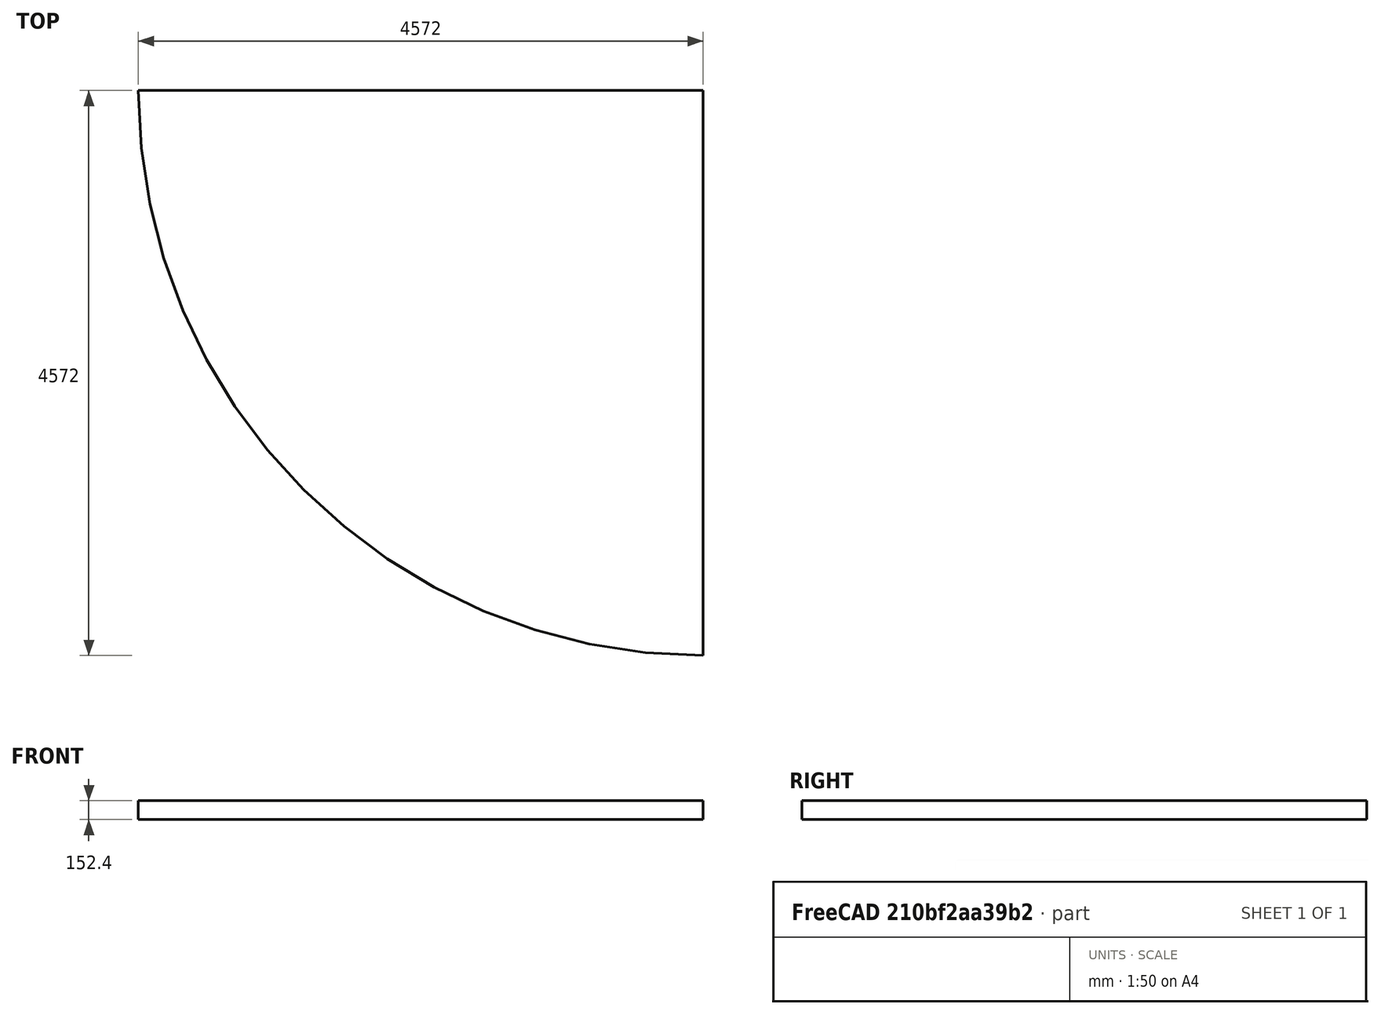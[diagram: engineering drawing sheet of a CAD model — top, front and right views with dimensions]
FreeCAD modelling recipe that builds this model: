
FCSTD DOCUMENT  (FreeCAD 0.20R29177 (Git))
Label: pad
License: All rights reserved
LicenseURL: http://en.wikipedia.org/wiki/All_rights_reserved
objects: Sketcher::SketchObject×1, PartDesign::Pad×1, PartDesign::Body×1
note: 4 computed .brp shape members not serialized (recipe doc carries the construction recipe); baked Part::Feature solids carry a one-line shape summary decoded from their .brp

FEATURE [Sketcher::SketchObject] Sketch
  FullyConstrained = true
  MapMode = 5
  Support = -> [XY_Plane]
  sketch-geometry (3):
    g0: LineSegment StartX=0 StartY=0 StartZ=0 EndX=1.5516e-12 EndY=-4572 EndZ=0
    g1: LineSegment StartX=0 StartY=0 StartZ=0 EndX=-4572 EndY=-6.39e-13 EndZ=0
    g2: ArcOfCircle CenterX=3.1739 CenterY=3.1739 CenterZ=0 NormalX=0 NormalY=0 NormalZ=1 AngleXU=0 Radius=4575.18 StartAngle=3.14229 EndAngle=4.7117
  constraints (9):
    c: PointOnObject(g0,g-2)
    c: Coincident(g1,g-1)
    c: PointOnObject(g1,g-1)
    c: Coincident(g0,g1)
    c: DistanceX(g1,g1) = 4572
    c: DistanceY(g0,g0) = 4572
    c: Coincident(g2,g1)
    c: Coincident(g2,g0)
    c: Radius(g2) = 4575.18
FEATURE [PartDesign::Pad] Pad
  Direction = (0,0,1)
  Length = 152.4
  Length2 = 9.525
  Profile = -> Sketch
  ReferenceAxis = -> Sketch [N_Axis]
  Type = 0
FEATURE [PartDesign::Body] Body
  Group = -> [Sketch,Pad]
  Origin = -> Origin
  Tip = -> Pad
